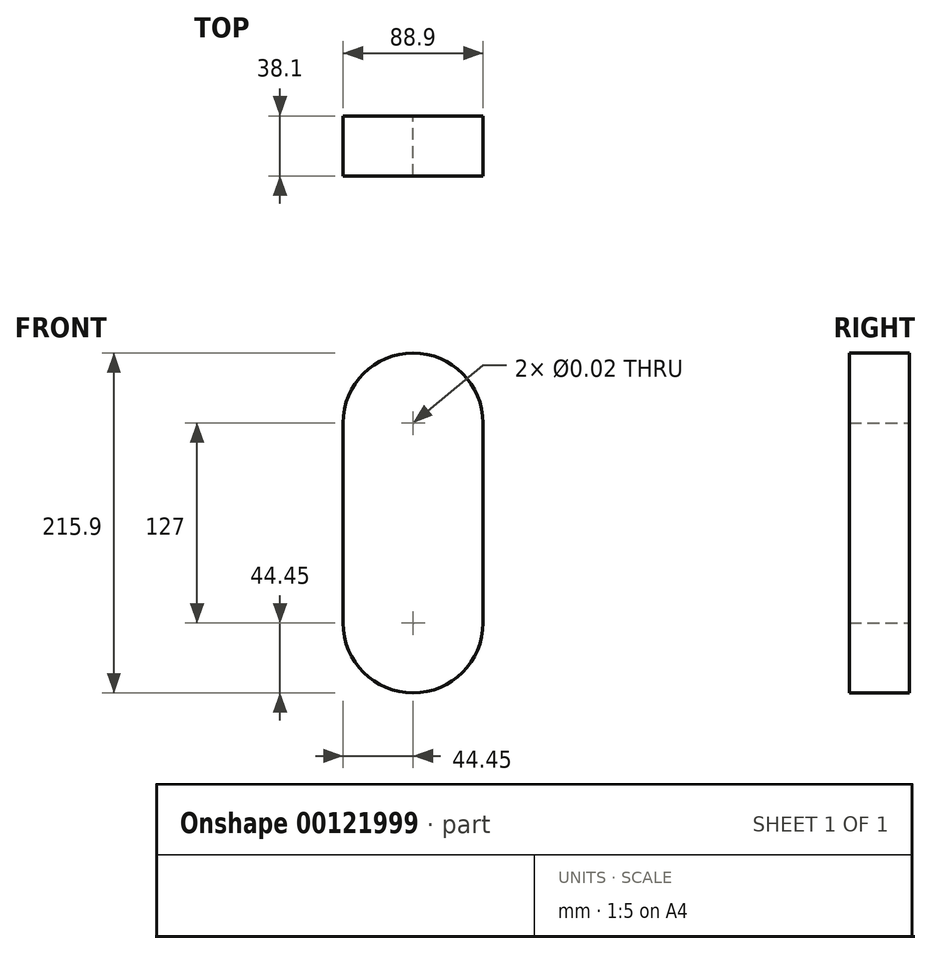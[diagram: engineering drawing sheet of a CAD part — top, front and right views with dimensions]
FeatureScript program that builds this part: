
annotation { "Feature Type Name" : "Feature", "Feature Type Description" : "" }
export const myFeature = defineFeature(function(context is Context, id is Id, definition is map)
    precondition{}
    {
        {
            var Q0;
            Q0=qCreatedBy(makeId("Front.planeOp"),FACE);
            var sketch = newSketch(context, id + "F0", { "sketchPlane" : qUnion([Q0])});
            skLineSegment(sketch, "E0.left", {"start": v(44.45, 63.5) * mm, "end": v(44.45, -63.5) * mm});
            skLineSegment(sketch, "E0.right", {"start": v(-44.45, 63.5) * mm, "end": v(-44.45, -63.5) * mm});
            skPoint(sketch, "E0.middle", {"position": v(0, 0) * mm});
            skArc(sketch, "E1", {"start": v(44.45, 63.5) * mm, "mid": v(0, 107.95) * mm, "end": v(-44.45, 63.5) * mm});
            skArc(sketch, "E2", {"start": v(-44.45, -63.5) * mm, "mid": v(0, -107.95) * mm, "end": v(44.45, -63.5) * mm});
            skLineSegment(sketch, "E3", {"start": v(-44.45, 63.5) * mm, "end": v(44.45, 63.5) * mm, "construction": true});
            skSolve(sketch);
        }
        {
            var Q0;
            Q0 = qSketchRegion(id + "F0", true);
            extrude(context, id + "F1", {"entities" : qUnion([Q0]), "depth" : 38.1 * mm});
        }
        {
            var Q0;
            Q0=sQuery(id+"F0.wireOp",VERTEX,"E1.center");
            var Q1;
            Q1=sQuery(id+"F0.wireOp",VERTEX,"E2.center");
            var Q2;
            Q2=makeQuery(id+"F1.opExtrude","SWEPT_BODY",BODY,{"disambiguationData":[OSD([sQuery(id+"F0.wireOp",EDGE,"E0.left"),sQuery(id+"F0.wireOp",EDGE,"E0.right"),sQuery(id+"F0.wireOp",EDGE,"E1"),sQuery(id+"F0.wireOp",EDGE,"E2")])]});
            hole(context, id + "F2", {"style" : HoleStyle.SIMPLE, "endStyle" : HoleEndStyle.THROUGH, "oppositeDirection" : true, "standardTappedOrClearance" : lookupTablePath({ "standard" : "ANSI", "size" : "1/2 (0.5)", "type" : "Drilled" }), "standardBlindInLast" : lookupTablePath({ "standard" : "ANSI", "size" : "1/2", "type" : "Drilled" }), "holeDiameter" : 1 / 50.8 * mm, "locations" : qUnion([Q0, Q1]), "scope" : qUnion([Q2]), "isTappedThrough" : true});
        }
    });
